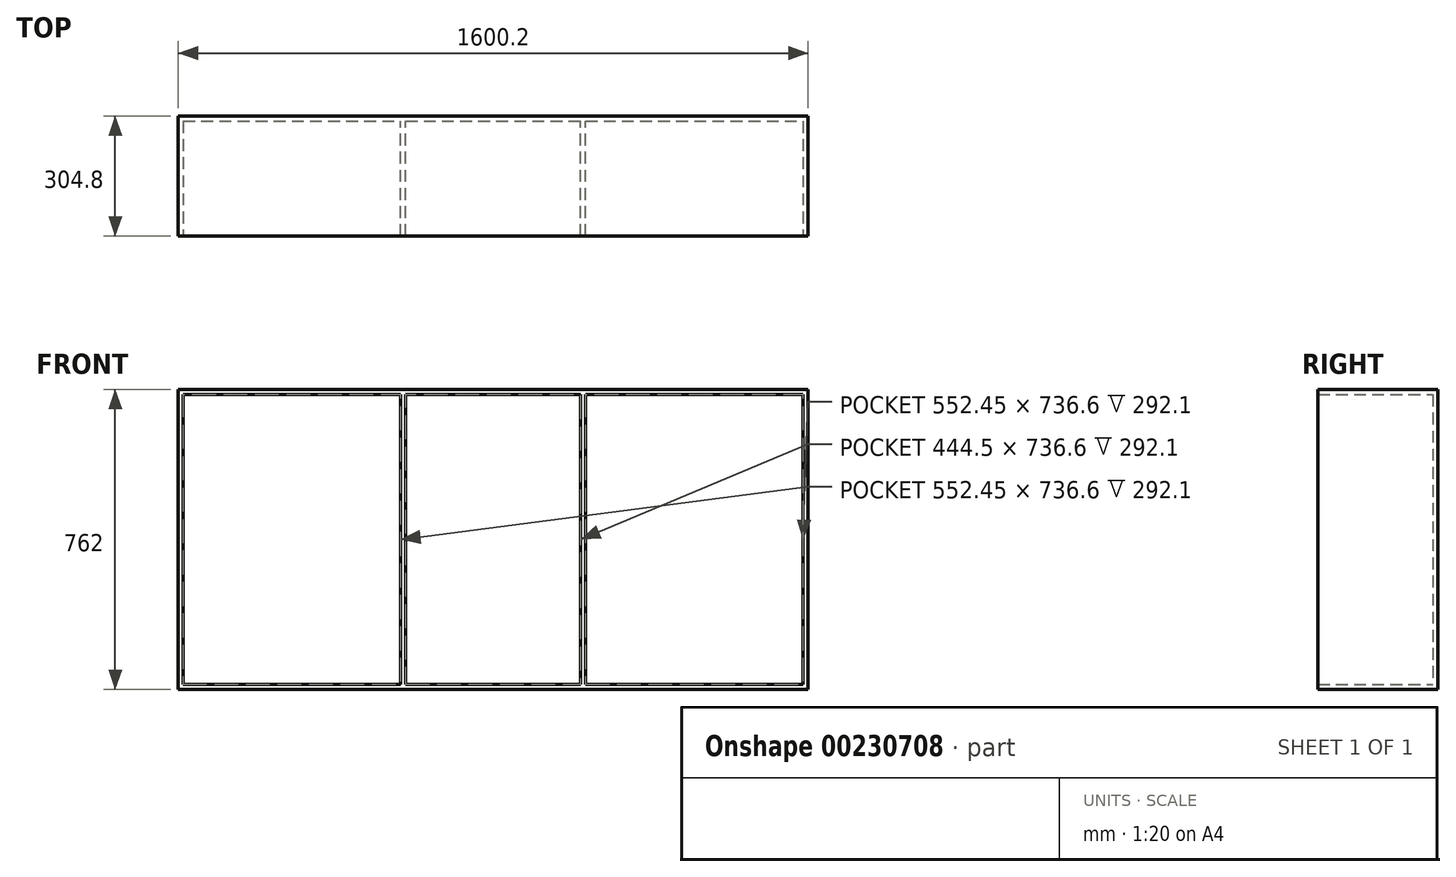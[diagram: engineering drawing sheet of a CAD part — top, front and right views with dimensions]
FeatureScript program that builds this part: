
annotation { "Feature Type Name" : "Feature", "Feature Type Description" : "" }
export const myFeature = defineFeature(function(context is Context, id is Id, definition is map)
    precondition{}
    {
        {
            var Q0;
            Q0=qCreatedBy(makeId("Front.planeOp"),FACE);
            var sketch = newSketch(context, id + "F0", { "sketchPlane" : qUnion([Q0])});
            skLineSegment(sketch, "E0.bottom", {"start": v(-800.1, 381) * mm, "end": v(800.1, 381) * mm});
            skLineSegment(sketch, "E0.top", {"start": v(-800.1, -381) * mm, "end": v(800.1, -381) * mm});
            skLineSegment(sketch, "E0.left", {"start": v(-800.1, 381) * mm, "end": v(-800.1, -381) * mm});
            skLineSegment(sketch, "E0.right", {"start": v(800.1, 381) * mm, "end": v(800.1, -381) * mm});
            skPoint(sketch, "E0.middle", {"position": v(0, 0) * mm});
            skSolve(sketch);
        }
        {
            var Q0;
            Q0=makeQuery(id+"F0.imprint","IMPRINT",FACE,{"disambiguationData":[TD([[makeQuery(id+"F0.imprint","IMPRINT",EDGE,{"derivedFrom":sQuery(id+"F0.wireOp",EDGE,"E0.bottom")}),-1.0]])]});
            extrude(context, id + "F1", {"entities" : qUnion([Q0]), "oppositeDirection" : true, "depth" : 304.8 * mm});
        }
        {
            var Q0;
            Q0=makeQuery(id+"F1.opExtrude","CAP_FACE",FACE,{"disambiguationData":[OSD([sQuery(id+"F0.wireOp",EDGE,"E0.bottom"),sQuery(id+"F0.wireOp",EDGE,"E0.top"),sQuery(id+"F0.wireOp",EDGE,"E0.left"),sQuery(id+"F0.wireOp",EDGE,"E0.right")])],"isStart":true});
            shell(context, id + "F2", {"entities" : qUnion([Q0]), "thickness" : 12.7 * mm});
        }
        {
            var Q0;
            Q0=makeQuery(id+"F2.opShell","OFFSET_FACE",FACE,{"disambiguationData":[OSD([sQuery(id+"F0.wireOp",EDGE,"E0.bottom"),sQuery(id+"F0.wireOp",EDGE,"E0.top"),sQuery(id+"F0.wireOp",EDGE,"E0.left"),sQuery(id+"F0.wireOp",EDGE,"E0.right")])]});
            var sketch = newSketch(context, id + "F3", { "sketchPlane" : qUnion([Q0])});
            skLineSegment(sketch, "E1.bottom", {"start": v(-234.95, 368.3) * mm, "end": v(-222.25, 368.3) * mm});
            skLineSegment(sketch, "E1.top", {"start": v(-234.95, -368.3) * mm, "end": v(-222.25, -368.3) * mm});
            skLineSegment(sketch, "E1.left", {"start": v(-234.95, 368.3) * mm, "end": v(-234.95, -368.3) * mm});
            skLineSegment(sketch, "E1.right", {"start": v(-222.25, 368.3) * mm, "end": v(-222.25, -368.3) * mm});
            skLineSegment(sketch, "E2.bottom", {"start": v(222.25, 368.3) * mm, "end": v(234.95, 368.3) * mm});
            skLineSegment(sketch, "E2.top", {"start": v(222.25, -368.3) * mm, "end": v(234.95, -368.3) * mm});
            skLineSegment(sketch, "E2.left", {"start": v(222.25, 368.3) * mm, "end": v(222.25, -368.3) * mm});
            skLineSegment(sketch, "E2.right", {"start": v(234.95, 368.3) * mm, "end": v(234.95, -368.3) * mm});
            skSolve(sketch);
        }
        {
            var Q0;
            Q0=makeQuery(id+"F3.imprint","IMPRINT",FACE,{"disambiguationData":[TD([[makeQuery(id+"F3.imprint","IMPRINT",EDGE,{"derivedFrom":sQuery(id+"F3.wireOp",EDGE,"E1.bottom")}),-1.0]])]});
            var Q1;
            Q1=makeQuery(id+"F3.imprint","IMPRINT",FACE,{"disambiguationData":[TD([[makeQuery(id+"F3.imprint","IMPRINT",EDGE,{"derivedFrom":sQuery(id+"F3.wireOp",EDGE,"E2.bottom")}),-1.0]])]});
            extrude(context, id + "F4", {"entities" : qUnion([Q0, Q1]), "operationType" : NewBodyOperationType.ADD, "depth" : 292.1 * mm});
        }
    });
